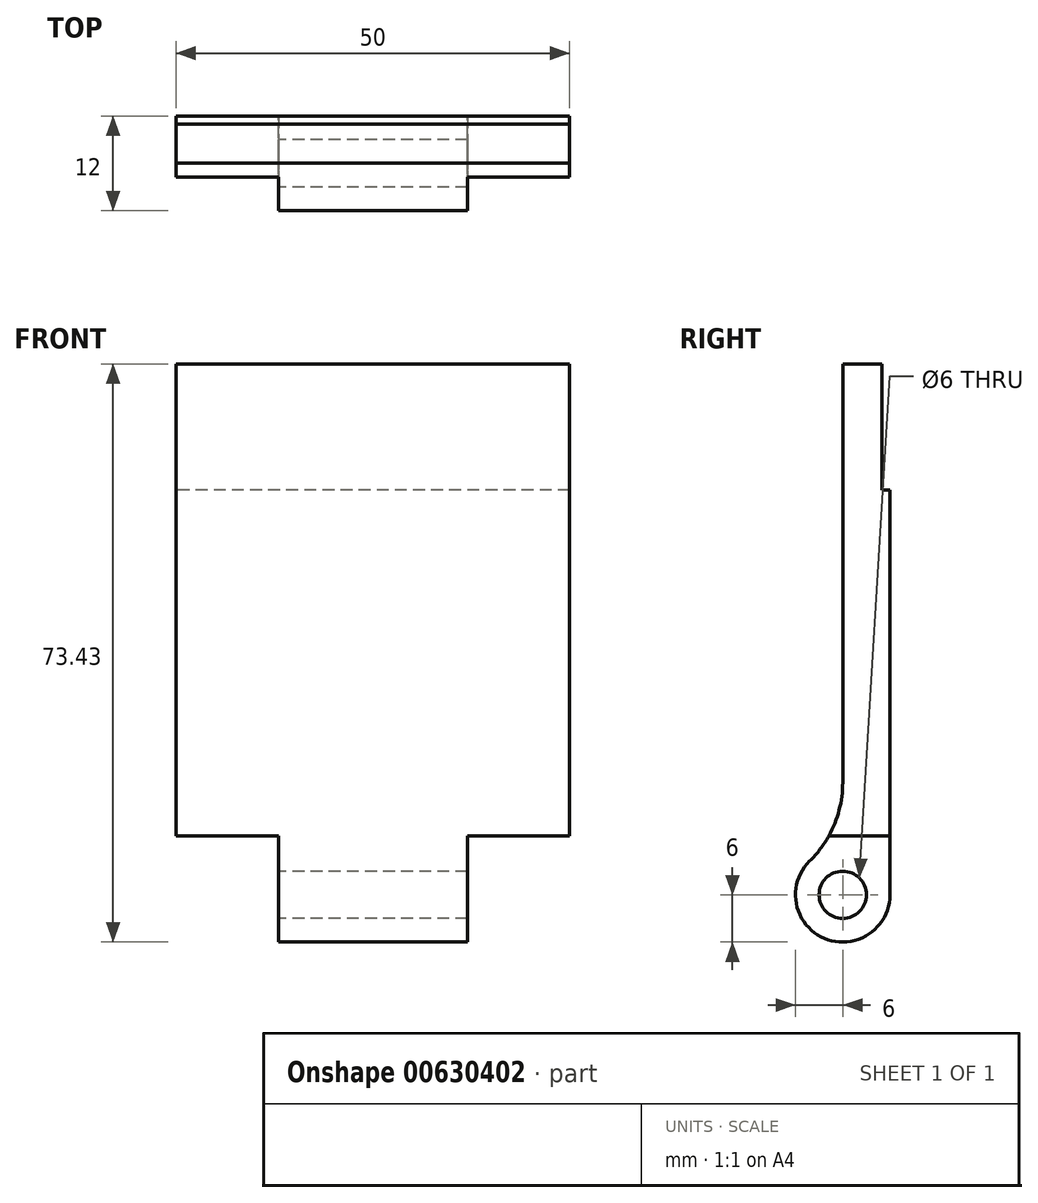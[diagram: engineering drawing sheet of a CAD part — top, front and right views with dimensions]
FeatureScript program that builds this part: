
annotation { "Feature Type Name" : "Feature", "Feature Type Description" : "" }
export const myFeature = defineFeature(function(context is Context, id is Id, definition is map)
    precondition{}
    {
        {
            var Q0;
            Q0=qCreatedBy(makeId("Right.planeOp"),FACE);
            var sketch = newSketch(context, id + "F0", { "sketchPlane" : qUnion([Q0])});
            skArc(sketch, "E0", {"start": v(0, 6) * mm, "mid": v(-4.24, -4.24) * mm, "end": v(6, 0) * mm});
            skCircle(sketch, "E1", {"center": v(0, 0) * mm, "radius": 3 * mm});
            skLineSegment(sketch, "E2", {"start": v(0, 6) * mm, "end": v(0, 67.43) * mm});
            skLineSegment(sketch, "E3", {"start": v(0, 67.43) * mm, "end": v(6, 67.43) * mm});
            skLineSegment(sketch, "E4", {"start": v(6, 67.43) * mm, "end": v(6, 0) * mm});
            skSolve(sketch);
        }
        {
            var Q0;
            Q0 = qSketchRegion(id + "F0", true);
            extrude(context, id + "F1", {"entities" : qUnion([Q0]), "endBound" : BoundingType.SYMMETRIC, "depth" : 50 * mm, "offsetDistance" : 25 * mm});
        }
        {
            var Q0;
            Q0=qCreatedBy(makeId("Front.planeOp"),FACE);
            var sketch = newSketch(context, id + "F2", { "sketchPlane" : qUnion([Q0])});
            skLineSegment(sketch, "E5.bottom", {"start": v(-12, -7.5) * mm, "end": v(-25, -7.5) * mm});
            skLineSegment(sketch, "E5.top", {"start": v(-12, 7.5) * mm, "end": v(-25, 7.5) * mm});
            skLineSegment(sketch, "E5.left", {"start": v(-12, -7.5) * mm, "end": v(-12, 7.5) * mm});
            skLineSegment(sketch, "E5.right", {"start": v(-25, -7.5) * mm, "end": v(-25, 7.5) * mm});
            skPoint(sketch, "E5.middle", {"position": v(-18.5, 0) * mm});
            skLineSegment(sketch, "E6.bottom", {"start": v(25, -7.5) * mm, "end": v(12, -7.5) * mm});
            skLineSegment(sketch, "E6.top", {"start": v(25, 7.5) * mm, "end": v(12, 7.5) * mm});
            skLineSegment(sketch, "E6.left", {"start": v(25, -7.5) * mm, "end": v(25, 7.5) * mm});
            skLineSegment(sketch, "E6.right", {"start": v(12, -7.5) * mm, "end": v(12, 7.5) * mm});
            skPoint(sketch, "E6.middle", {"position": v(18.5, 0) * mm});
            skSolve(sketch);
        }
        {
            var Q0;
            Q0 = qSketchRegion(id + "F2", true);
            extrude(context, id + "F3", {"entities" : qUnion([Q0]), "operationType" : NewBodyOperationType.REMOVE, "endBound" : BoundingType.SYMMETRIC, "oppositeDirection" : true, "depth" : 25 * mm, "offsetDistance" : 25 * mm});
        }
        {
            var Q0;
            Q0=qCreatedBy(makeId("Right.planeOp"),FACE);
            var sketch = newSketch(context, id + "F4", { "sketchPlane" : qUnion([Q0])});
            skLineSegment(sketch, "E7.bottom", {"start": v(6, 51.43) * mm, "end": v(5, 51.43) * mm});
            skLineSegment(sketch, "E7.top", {"start": v(6, 67.43) * mm, "end": v(5, 67.43) * mm});
            skLineSegment(sketch, "E7.left", {"start": v(6, 51.43) * mm, "end": v(6, 67.43) * mm});
            skLineSegment(sketch, "E7.right", {"start": v(5, 51.43) * mm, "end": v(5, 67.43) * mm});
            skSolve(sketch);
        }
        {
            var Q0;
            Q0 = qSketchRegion(id + "F4", true);
            extrude(context, id + "F5", {"entities" : qUnion([Q0]), "operationType" : NewBodyOperationType.REMOVE, "endBound" : BoundingType.SYMMETRIC, "depth" : 60 * mm, "offsetDistance" : 25 * mm});
        }
        {
            var Q0;
            Q0=makeQuery(id+"F1.opExtrude","SWEPT_EDGE",EDGE,{"disambiguationData":[OSD([sQuery(id+"F0.wireOp",EDGE,"E0"),sQuery(id+"F0.wireOp",EDGE,"E2")])]});
            fillet(context, id + "F6", {"entities" : qUnion([Q0]), "radius" : 14 * mm, "tangentPropagation" : true, "allowEdgeOverflow" : false});
        }
    });
